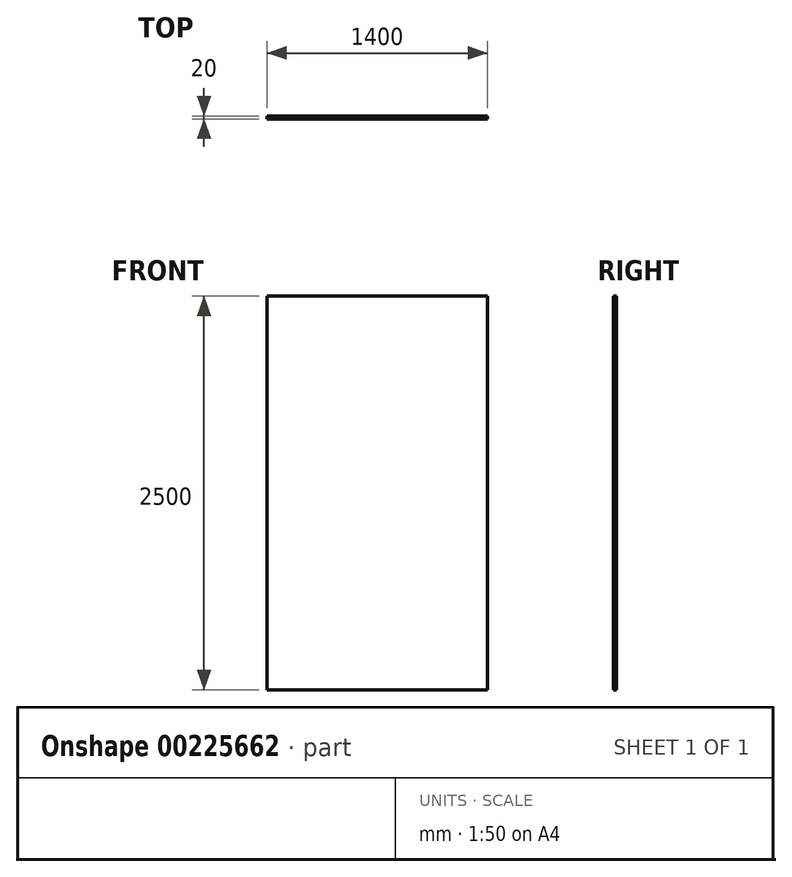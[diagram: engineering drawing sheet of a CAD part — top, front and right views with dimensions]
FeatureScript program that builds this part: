
annotation { "Feature Type Name" : "Feature", "Feature Type Description" : "" }
export const myFeature = defineFeature(function(context is Context, id is Id, definition is map)
    precondition{}
    {
        {
            var Q0;
            Q0=qCreatedBy(makeId("Front.planeOp"),FACE);
            var sketch = newSketch(context, id + "F0", { "sketchPlane" : qUnion([Q0])});
            skLineSegment(sketch, "E0.bottom", {"start": v(0, 0) * mm, "end": v(1400, 0) * mm});
            skLineSegment(sketch, "E0.top", {"start": v(0, 2500) * mm, "end": v(1400, 2500) * mm});
            skLineSegment(sketch, "E0.left", {"start": v(0, 0) * mm, "end": v(0, 2500) * mm});
            skLineSegment(sketch, "E0.right", {"start": v(1400, 0) * mm, "end": v(1400, 2500) * mm});
            skSolve(sketch);
        }
        {
            var Q0;
            Q0 = qSketchRegion(id + "F0", true);
            extrude(context, id + "F1", {"entities" : qUnion([Q0]), "depth" : 20 * mm});
        }
    });
